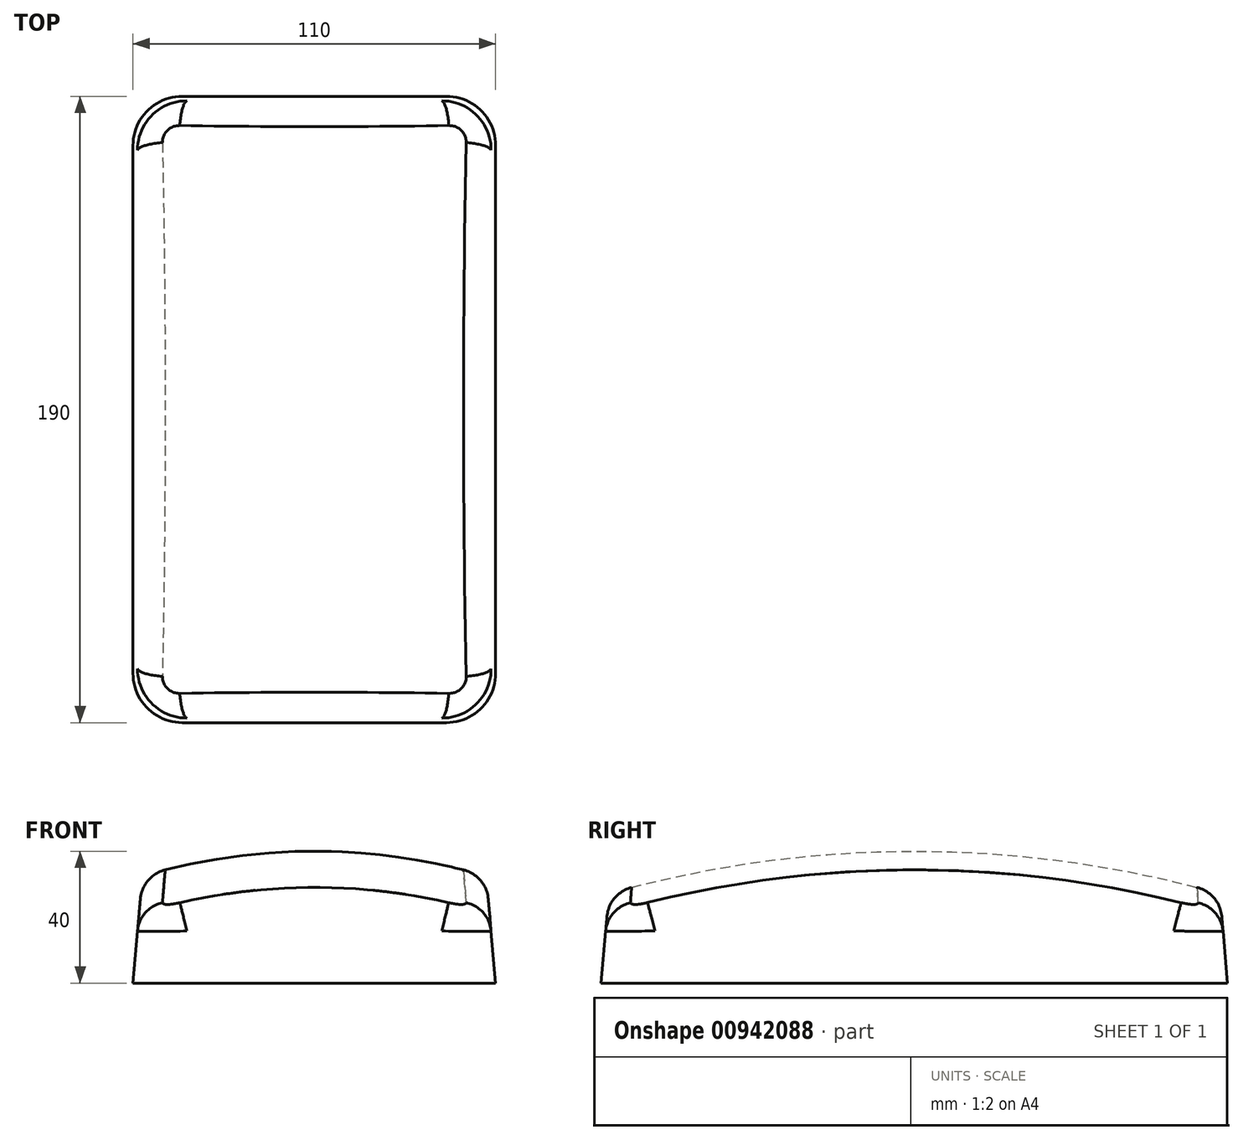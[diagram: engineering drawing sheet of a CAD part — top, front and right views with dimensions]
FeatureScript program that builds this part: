
annotation { "Feature Type Name" : "Feature", "Feature Type Description" : "" }
export const myFeature = defineFeature(function(context is Context, id is Id, definition is map)
    precondition{}
    {
        {
            var Q0;
            Q0=qCreatedBy(makeId("Front.planeOp"),FACE);
            cPlane(context, id + "F0", {"entities" : qUnion([Q0]), "cplaneType" : CPlaneType.OFFSET, "offset" : 100 * mm, "width" : 150 * mm, "height" : 150 * mm});
        }
        {
            var Q0;
            Q0=qCreatedBy(makeId("Front.planeOp"),FACE);
            cPlane(context, id + "F1", {"entities" : qUnion([Q0]), "cplaneType" : CPlaneType.OFFSET, "offset" : 100 * mm, "oppositeDirection" : true, "width" : 150 * mm, "height" : 150 * mm});
        }
        {
            var Q0;
            Q0=qCreatedBy(makeId("Right.planeOp"),FACE);
            cPlane(context, id + "F2", {"entities" : qUnion([Q0]), "cplaneType" : CPlaneType.OFFSET, "offset" : 60 * mm, "width" : 150 * mm, "height" : 150 * mm});
        }
        {
            var Q0;
            Q0=qCreatedBy(makeId("Right.planeOp"),FACE);
            cPlane(context, id + "F3", {"entities" : qUnion([Q0]), "cplaneType" : CPlaneType.OFFSET, "offset" : 60 * mm, "oppositeDirection" : true, "width" : 150 * mm, "height" : 150 * mm});
        }
        {
            var Q0;
            Q0=qCreatedBy(id+"F2.planeOp",FACE);
            var sketch = newSketch(context, id + "F4", { "sketchPlane" : qUnion([Q0])});
            skLineSegment(sketch, "E0", {"start": v(-100, 0) * mm, "end": v(100, 0) * mm, "construction": true});
            skLineSegment(sketch, "E1", {"start": v(0, 0) * mm, "end": v(0, 38.29) * mm, "construction": true});
            skLineSegment(sketch, "E2", {"start": v(-100, 0) * mm, "end": v(-100, 15) * mm, "construction": true});
            skLineSegment(sketch, "E3", {"start": v(-100, 15) * mm, "end": v(100, 15) * mm, "construction": true});
            skLineSegment(sketch, "E4", {"start": v(100, 15) * mm, "end": v(100, 0) * mm, "construction": true});
            skArc(sketch, "E5", {"start": v(100, 15) * mm, "mid": v(0, 30) * mm, "end": v(-100, 15) * mm});
            skLineSegment(sketch, "E6", {"start": v(-61.22, 30) * mm, "end": v(47.89, 30) * mm, "construction": true});
            skSolve(sketch);
        }
        {
            var Q0;
            Q0=qCreatedBy(id+"F3.planeOp",FACE);
            var sketch = newSketch(context, id + "F5", { "sketchPlane" : qUnion([Q0])});
            skLineSegment(sketch, "E7.0", {"start": v(-100, 0) * mm, "end": v(100, 0) * mm, "construction": true});
            skArc(sketch, "E8.0", {"start": v(100, 15) * mm, "mid": v(0, 30) * mm, "end": v(-100, 15) * mm});
            skLineSegment(sketch, "E9.0", {"start": v(-100, 0) * mm, "end": v(-100, 15) * mm, "construction": true});
            skLineSegment(sketch, "E10.0", {"start": v(100, 15) * mm, "end": v(100, 0) * mm, "construction": true});
            skLineSegment(sketch, "E11.0", {"start": v(0, 0) * mm, "end": v(0, 38.29) * mm, "construction": true});
            skSolve(sketch);
        }
        {
            var Q0;
            Q0=qCreatedBy(makeId("Right.planeOp"),FACE);
            var sketch = newSketch(context, id + "F6", { "sketchPlane" : qUnion([Q0])});
            skLineSegment(sketch, "E12.0", {"start": v(-100, 0) * mm, "end": v(100, 0) * mm, "construction": true});
            skLineSegment(sketch, "E13", {"start": v(-100, 0) * mm, "end": v(-100, 25) * mm, "construction": true});
            skLineSegment(sketch, "E14", {"start": v(-100, 25) * mm, "end": v(100, 25) * mm, "construction": true});
            skLineSegment(sketch, "E15", {"start": v(100, 25) * mm, "end": v(100, 0) * mm, "construction": true});
            skArc(sketch, "E16", {"start": v(100, 25) * mm, "mid": v(0, 40) * mm, "end": v(-100, 25) * mm});
            skSolve(sketch);
        }
        {
            var Q0;
            Q0=qCreatedBy(id+"F0.planeOp",FACE);
            var sketch = newSketch(context, id + "F7", { "sketchPlane" : qUnion([Q0])});
            skArc(sketch, "E17", {"start": v(60, 15) * mm, "mid": v(0, 25) * mm, "end": v(-60, 15) * mm});
            skSolve(sketch);
        }
        {
            var Q0;
            Q0=qCreatedBy(id+"F1.planeOp",FACE);
            var sketch = newSketch(context, id + "F8", { "sketchPlane" : qUnion([Q0])});
            skArc(sketch, "E18", {"start": v(60, 15) * mm, "mid": v(0, 25) * mm, "end": v(-60, 15) * mm});
            skSolve(sketch);
        }
        {
            var Q0;
            Q0=sQuery(id+"F7.wireOp",EDGE,"E17");
            var Q1;
            Q1=sQuery(id+"F4.wireOp",EDGE,"E5");
            var Q2;
            Q2=sQuery(id+"F6.wireOp",EDGE,"E16");
            var Q3;
            Q3=sQuery(id+"F5.wireOp",EDGE,"E8.0");
            var Q4;
            Q4=sQuery(id+"F8.wireOp",EDGE,"E18");
            loft(context, id + "F9", {"bodyType" : ToolBodyType.SURFACE, "addSections" : true, "spine" : qUnion([Q0]), "sectionCount" : 10, "addGuides" : true, "wireProfilesArray" : [{ "wireProfileEntities" : qUnion([Q1]) }, { "wireProfileEntities" : qUnion([Q2]) }, { "wireProfileEntities" : qUnion([Q3]) }], "guidesArray" : [{ "guideEntities" : qUnion([Q4]), "guideDerivativeType" : LoftGuideDerivativeType.DEFAULT, "guideDerivativeMagnitude" : 1 }]});
        }
        {
            var Q0;
            Q0=qCreatedBy(makeId("Top.planeOp"),FACE);
            var sketch = newSketch(context, id + "F10", { "sketchPlane" : qUnion([Q0])});
            skLineSegment(sketch, "E19.bottom", {"start": v(55, 95) * mm, "end": v(-55, 95) * mm});
            skLineSegment(sketch, "E19.top", {"start": v(55, -95) * mm, "end": v(-55, -95) * mm});
            skLineSegment(sketch, "E19.left", {"start": v(55, 95) * mm, "end": v(55, -95) * mm});
            skLineSegment(sketch, "E19.right", {"start": v(-55, 95) * mm, "end": v(-55, -95) * mm});
            skPoint(sketch, "E19.middle", {"position": v(0, 0) * mm});
            skSolve(sketch);
        }
        {
            var Q0;
            Q0 = qSketchRegion(id + "F10", true);
            var Q1;
            Q1=makeQuery(id+"F9.opLoft","SWEPT_FACE",FACE,{"disambiguationData":[OSD([sQuery(id+"F4.wireOp",VERTEX,"E5.end"),sQuery(id+"F4.wireOp",EDGE,"E5"),sQuery(id+"F5.wireOp",VERTEX,"E8.0.end"),sQuery(id+"F5.wireOp",EDGE,"E8.0"),sQuery(id+"F6.wireOp",VERTEX,"E16.end"),sQuery(id+"F6.wireOp",EDGE,"E16"),sQuery(id+"F8.wireOp",EDGE,"E18")])]});
            extrude(context, id + "F11", {"entities" : qUnion([Q0]), "endBound" : BoundingType.UP_TO_SURFACE, "depth" : 25 * mm, "endBoundEntityFace" : qUnion([Q1]), "offsetDistance" : 25 * mm, "hasDraft" : true, "draftAngle" : 5 * degree, "draftPullDirection" : true});
        }
        {
            var Q0;
            Q0=makeQuery(id+"F11.opExtrude","SWEPT_EDGE",EDGE,{"disambiguationData":[OSD([sQuery(id+"F10.wireOp",EDGE,"E19.top"),sQuery(id+"F10.wireOp",EDGE,"E19.left")])]});
            var Q1;
            Q1=makeQuery(id+"F11.opExtrude","SWEPT_EDGE",EDGE,{"disambiguationData":[OSD([sQuery(id+"F10.wireOp",EDGE,"E19.top"),sQuery(id+"F10.wireOp",EDGE,"E19.right")])]});
            var Q2;
            Q2=makeQuery(id+"F11.opExtrude","SWEPT_EDGE",EDGE,{"disambiguationData":[OSD([sQuery(id+"F10.wireOp",EDGE,"E19.bottom"),sQuery(id+"F10.wireOp",EDGE,"E19.left")])]});
            var Q3;
            Q3=makeQuery(id+"F11.opExtrude","SWEPT_EDGE",EDGE,{"disambiguationData":[OSD([sQuery(id+"F10.wireOp",EDGE,"E19.bottom"),sQuery(id+"F10.wireOp",EDGE,"E19.right")])]});
            fillet(context, id + "F12", {"entities" : qUnion([Q0, Q1, Q2, Q3]), "radius" : 15 * mm, "tangentPropagation" : true, "allowEdgeOverflow" : false});
        }
        {
            var Q0;
            Q0=makeQuery(id+"F11.opExtrude","CAP_FACE",FACE,{"disambiguationData":[OSD([sQuery(id+"F10.wireOp",EDGE,"E19.bottom"),sQuery(id+"F10.wireOp",EDGE,"E19.top"),sQuery(id+"F10.wireOp",EDGE,"E19.left"),sQuery(id+"F10.wireOp",EDGE,"E19.right")])],"isStart":false});
            fillet(context, id + "F13", {"entities" : qUnion([Q0]), "radius" : 10 * mm, "tangentPropagation" : true, "allowEdgeOverflow" : false});
        }
        {
            var Q0;
            Q0=makeQuery(id+"F11.opExtrude","SWEPT_BODY",BODY,{"disambiguationData":[OSD([sQuery(id+"F10.wireOp",EDGE,"E19.bottom"),sQuery(id+"F10.wireOp",EDGE,"E19.top"),sQuery(id+"F10.wireOp",EDGE,"E19.left"),sQuery(id+"F10.wireOp",EDGE,"E19.right")])]});
            transform(context, id + "F14", {"entities" : qUnion([Q0]), "transformType" : TransformType.TRANSLATION_3D, "dx" : 0 * mm, "dy" : 0 * mm, "dz" : -80 * mm, "makeCopy" : false});
        }
    });
